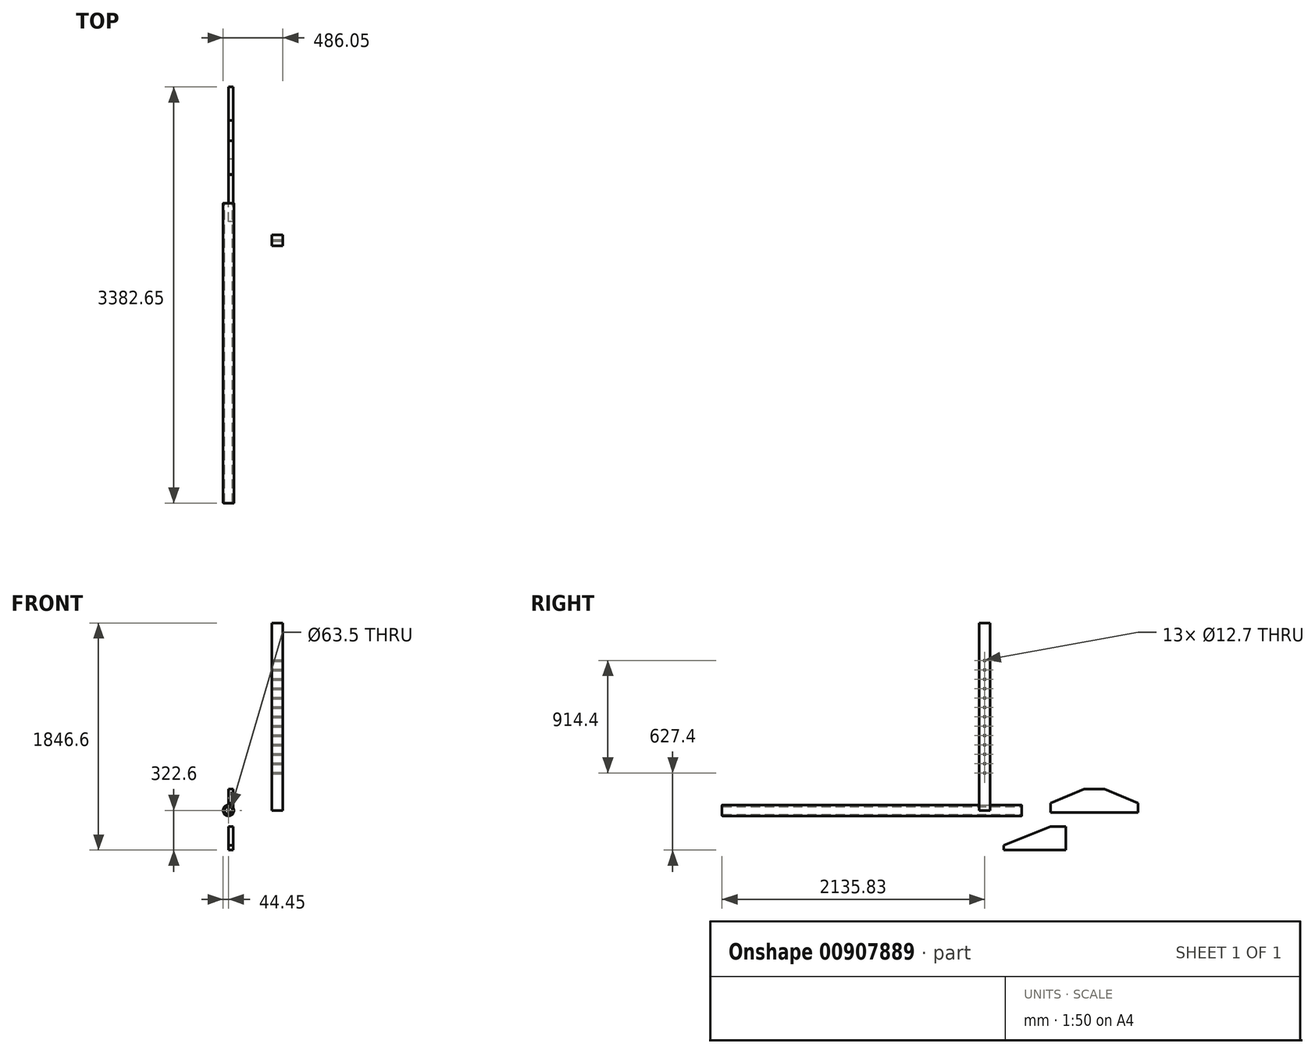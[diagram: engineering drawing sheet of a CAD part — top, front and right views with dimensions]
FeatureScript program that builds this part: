
annotation { "Feature Type Name" : "Feature", "Feature Type Description" : "" }
export const myFeature = defineFeature(function(context is Context, id is Id, definition is map)
    precondition{}
    {
        {
            var Q0;
            Q0=qCreatedBy(makeId("Front.planeOp"),FACE);
            var sketch = newSketch(context, id + "F0", { "sketchPlane" : qUnion([Q0])});
            skCircle(sketch, "E0", {"center": v(0, 0) * mm, "radius": 44.45 * mm});
            skSolve(sketch);
        }
        {
            var Q0;
            Q0=makeQuery(id+"F0.imprint","IMPRINT",FACE,{"disambiguationData":[TD([[makeQuery(id+"F0.imprint","IMPRINT",EDGE,{"derivedFrom":sQuery(id+"F0.wireOp",EDGE,"E0")}),1.0]])]});
            extrude(context, id + "F1", {"entities" : qUnion([Q0]), "depth" : 2438.4 * mm, "offsetDistance" : 25.4 * mm});
        }
        {
            var Q0;
            Q0=qCreatedBy(makeId("Top.planeOp"),FACE);
            var sketch = newSketch(context, id + "F2", { "sketchPlane" : qUnion([Q0])});
            skLineSegment(sketch, "E1.bottom", {"start": v(352.7, -258.12) * mm, "end": v(441.6, -258.12) * mm});
            skLineSegment(sketch, "E1.top", {"start": v(352.7, -347.02) * mm, "end": v(441.6, -347.02) * mm});
            skLineSegment(sketch, "E1.left", {"start": v(352.7, -258.12) * mm, "end": v(352.7, -347.02) * mm});
            skLineSegment(sketch, "E1.right", {"start": v(441.6, -258.12) * mm, "end": v(441.6, -347.02) * mm});
            skSolve(sketch);
        }
        {
            var Q0;
            Q0=makeQuery(id+"F2.imprint","IMPRINT",FACE,{"disambiguationData":[TD([[makeQuery(id+"F2.imprint","IMPRINT",EDGE,{"derivedFrom":sQuery(id+"F2.wireOp",EDGE,"E1.bottom")}),-1.0]])]});
            extrude(context, id + "F3", {"entities" : qUnion([Q0]), "depth" : 1524 * mm, "offsetDistance" : 25.4 * mm});
        }
        {
            var Q0;
            Q0=qCreatedBy(makeId("Right.planeOp"),FACE);
            var sketch = newSketch(context, id + "F4", { "sketchPlane" : qUnion([Q0])});
            skLineSegment(sketch, "E2", {"start": v(232.24, -132.1) * mm, "end": v(359.24, -132.1) * mm});
            skLineSegment(sketch, "E3", {"start": v(359.24, -132.1) * mm, "end": v(359.24, -322.6) * mm});
            skLineSegment(sketch, "E4", {"start": v(-148.76, -322.6) * mm, "end": v(359.24, -322.6) * mm});
            skLineSegment(sketch, "E5", {"start": v(-148.76, -322.6) * mm, "end": v(-148.76, -284.5) * mm});
            skLineSegment(sketch, "E6", {"start": v(-148.76, -284.5) * mm, "end": v(232.24, -132.1) * mm});
            skSolve(sketch);
        }
        {
            var Q0;
            Q0=makeQuery(id+"F4.imprint","IMPRINT",FACE,{"disambiguationData":[TD([[makeQuery(id+"F4.imprint","IMPRINT",EDGE,{"derivedFrom":sQuery(id+"F4.wireOp",EDGE,"E2")}),-1.0]])]});
            extrude(context, id + "F5", {"entities" : qUnion([Q0]), "depth" : 38.1 * mm, "offsetDistance" : 25.4 * mm});
        }
        {
            var Q0;
            Q0=makeQuery(id+"F3.opExtrude","SWEPT_FACE",FACE,{"disambiguationData":[OSD([sQuery(id+"F2.wireOp",EDGE,"E1.right")])]});
            var sketch = newSketch(context, id + "F6", { "sketchPlane" : qUnion([Q0])});
            skCircle(sketch, "E7", {"center": v(-302.57, 304.8) * mm, "radius": 6.35 * mm});
            skCircle(sketch, "E8.0.1.0", {"center": v(-302.57, 381) * mm, "radius": 6.35 * mm});
            skCircle(sketch, "E8.0.2.0", {"center": v(-302.57, 457.2) * mm, "radius": 6.35 * mm});
            skCircle(sketch, "E8.0.3.0", {"center": v(-302.57, 533.4) * mm, "radius": 6.35 * mm});
            skCircle(sketch, "E8.0.4.0", {"center": v(-302.57, 609.6) * mm, "radius": 6.35 * mm});
            skCircle(sketch, "E8.0.5.0", {"center": v(-302.57, 685.8) * mm, "radius": 6.35 * mm});
            skCircle(sketch, "E8.0.6.0", {"center": v(-302.57, 762) * mm, "radius": 6.35 * mm});
            skCircle(sketch, "E8.0.7.0", {"center": v(-302.57, 838.2) * mm, "radius": 6.35 * mm});
            skCircle(sketch, "E8.0.8.0", {"center": v(-302.57, 914.4) * mm, "radius": 6.35 * mm});
            skLineSegment(sketch, "E8.direction1", {"start": v(-302.57, 304.8) * mm, "end": v(-270.82, 304.8) * mm, "construction": true});
            skLineSegment(sketch, "E8.direction2", {"start": v(-302.57, 304.8) * mm, "end": v(-302.57, 381) * mm, "construction": true});
            skCircle(sketch, "E9.0.0.9", {"center": v(-302.57, 990.6) * mm, "radius": 6.35 * mm});
            skCircle(sketch, "E9.0.0.10", {"center": v(-302.57, 1066.8) * mm, "radius": 6.35 * mm});
            skCircle(sketch, "E9.0.0.11", {"center": v(-302.57, 1143) * mm, "radius": 6.35 * mm});
            skCircle(sketch, "E10.0.0.12", {"center": v(-302.57, 1219.2) * mm, "radius": 6.35 * mm});
            skSolve(sketch);
        }
        {
            var Q0;
            Q0 = qSketchRegion(id + "F6", true);
            extrude(context, id + "F7", {"entities" : qUnion([Q0]), "operationType" : NewBodyOperationType.REMOVE, "endBound" : BoundingType.UP_TO_NEXT, "oppositeDirection" : true, "depth" : 25.4 * mm, "offsetDistance" : 25.4 * mm});
        }
        {
            var Q0;
            Q0=makeQuery(id+"F1.opExtrude","CAP_FACE",FACE,{"disambiguationData":[OSD([sQuery(id+"F0.wireOp",EDGE,"E0")])],"isStart":true});
            var Q1;
            Q1=makeQuery(id+"F1.opExtrude","CAP_FACE",FACE,{"disambiguationData":[OSD([sQuery(id+"F0.wireOp",EDGE,"E0")])],"isStart":false});
            shell(context, id + "F8", {"entities" : qUnion([Q0, Q1]), "thickness" : 12.7 * mm});
        }
        {
            var Q0;
            Q0=makeQuery(id+"F8.opShell","OFFSET_FACE",FACE,{"disambiguationData":[OSD([sQuery(id+"F0.wireOp",EDGE,"E0")])]});
            var Q1;
            Q1=makeQuery(id+"F1.opExtrude","SWEPT_FACE",FACE,{"disambiguationData":[OSD([sQuery(id+"F0.wireOp",EDGE,"E0")])]});
            fillet(context, id + "F9", {"entities" : qUnion([Q0, Q1]), "radius" : 3.8 * mm, "tangentPropagation" : true, "allowEdgeOverflow" : false});
        }
        {
            var Q0;
            Q0=qCreatedBy(makeId("Right.planeOp"),FACE);
            var sketch = newSketch(context, id + "F10", { "sketchPlane" : qUnion([Q0])});
            skLineSegment(sketch, "E11", {"start": v(233.05, 58.43) * mm, "end": v(506.1, 172.73) * mm});
            skLineSegment(sketch, "E12", {"start": v(506.1, 172.73) * mm, "end": v(588.65, 172.73) * mm});
            skLineSegment(sketch, "E13", {"start": v(233.05, 58.43) * mm, "end": v(233.05, -17.77) * mm});
            skLineSegment(sketch, "E14", {"start": v(233.05, -17.77) * mm, "end": v(588.65, -17.77) * mm});
            skLineSegment(sketch, "E15", {"start": v(588.65, 172.73) * mm, "end": v(588.65, -17.77) * mm, "construction": true});
            skLineSegment(sketch, "E16.MirrorCS", {"start": v(671.2, 172.73) * mm, "end": v(588.65, 172.73) * mm});
            skLineSegment(sketch, "E17.MirrorCS", {"start": v(944.25, 58.43) * mm, "end": v(671.2, 172.73) * mm});
            skLineSegment(sketch, "E18.MirrorCS", {"start": v(944.25, 58.43) * mm, "end": v(944.25, -17.77) * mm});
            skLineSegment(sketch, "E19.MirrorCS", {"start": v(944.25, -17.77) * mm, "end": v(588.65, -17.77) * mm});
            skSolve(sketch);
        }
        {
            var Q0;
            Q0=makeQuery(id+"F10.imprint","IMPRINT",FACE,{"disambiguationData":[TD([[makeQuery(id+"F10.imprint","IMPRINT",EDGE,{"derivedFrom":sQuery(id+"F10.wireOp",EDGE,"E11")}),-1.0]])]});
            extrude(context, id + "F11", {"entities" : qUnion([Q0]), "depth" : 38.1 * mm, "offsetDistance" : 25.4 * mm});
        }
    });
